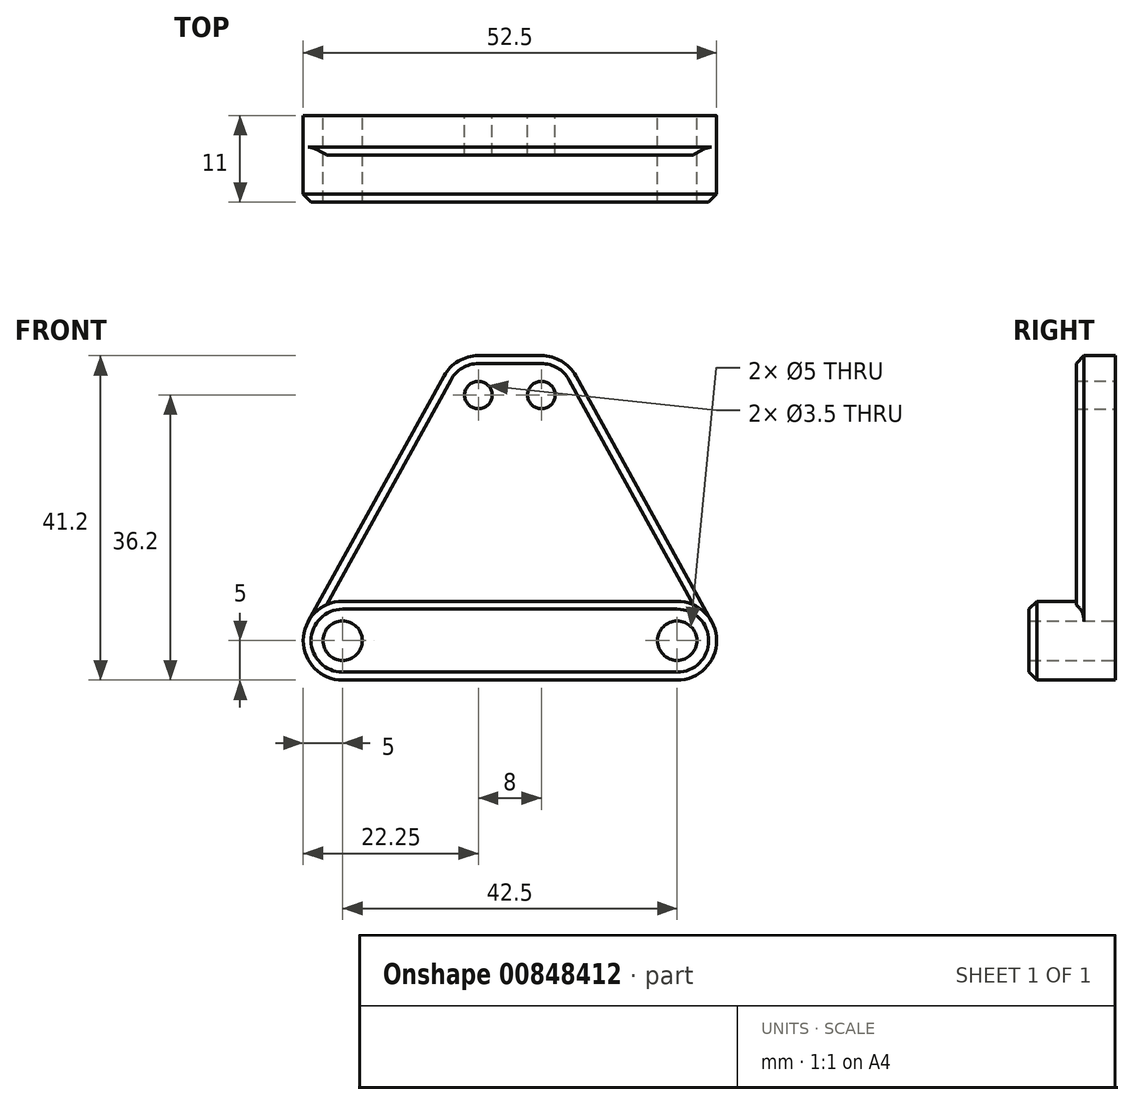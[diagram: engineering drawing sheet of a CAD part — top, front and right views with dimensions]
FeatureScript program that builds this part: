
annotation { "Feature Type Name" : "Feature", "Feature Type Description" : "" }
export const myFeature = defineFeature(function(context is Context, id is Id, definition is map)
    precondition{}
    {
        {
            var Q0;
            Q0=qCreatedBy(makeId("Front.planeOp"),FACE);
            var sketch = newSketch(context, id + "F0", { "sketchPlane" : qUnion([Q0])});
            skCircle(sketch, "E0", {"center": v(0, 0) * mm, "radius": 2.5 * mm});
            skCircle(sketch, "E1", {"center": v(42.5, 0) * mm, "radius": 2.5 * mm});
            skCircle(sketch, "E2", {"center": v(17.25, 31.2) * mm, "radius": 1.75 * mm});
            skCircle(sketch, "E3", {"center": v(25.25, 31.2) * mm, "radius": 1.75 * mm});
            skLineSegment(sketch, "E4", {"start": v(0, 0) * mm, "end": v(42.5, 0) * mm});
            skLineSegment(sketch, "E5", {"start": v(17.25, 31.2) * mm, "end": v(25.25, 31.2) * mm});
            skPoint(sketch, "E6", {"position": v(21.25, 31.2) * mm});
            skPoint(sketch, "E7", {"position": v(21.25, 0) * mm});
            skArc(sketch, "E8", {"start": v(-4.38, 2.42) * mm, "mid": v(-4.3, -2.54) * mm, "end": v(0, -5) * mm});
            skArc(sketch, "E9", {"start": v(42.5, -5) * mm, "mid": v(46.8, -2.54) * mm, "end": v(46.88, 2.42) * mm});
            skArc(sketch, "E10", {"start": v(17.25, 36.2) * mm, "mid": v(14.7, 35.5) * mm, "end": v(12.87, 33.62) * mm});
            skArc(sketch, "E11", {"start": v(29.63, 33.62) * mm, "mid": v(27.8, 35.5) * mm, "end": v(25.25, 36.2) * mm});
            skLineSegment(sketch, "E12", {"start": v(-4.38, 2.42) * mm, "end": v(12.87, 33.62) * mm});
            skLineSegment(sketch, "E13", {"start": v(17.25, 36.2) * mm, "end": v(25.25, 36.2) * mm});
            skLineSegment(sketch, "E14", {"start": v(29.63, 33.62) * mm, "end": v(46.88, 2.42) * mm});
            skLineSegment(sketch, "E15", {"start": v(42.5, -5) * mm, "end": v(0, -5) * mm});
            skSolve(sketch);
        }
        {
            var Q0;
            Q0=makeQuery(id+"F0.imprint","IMPRINT",FACE,{"disambiguationData":[TD([[makeQuery(id+"F0.imprint","IMPRINT",EDGE,{"derivedFrom":sQuery(id+"F0.wireOp",EDGE,"E0")}),-1.0]])]});
            extrude(context, id + "F1", {"entities" : qUnion([Q0]), "depth" : 5 * mm, "offsetDistance" : 25 * mm});
        }
        {
            var Q0;
            Q0=makeQuery(id+"F1.opExtrude","CAP_FACE",FACE,{"disambiguationData":[OSD([sQuery(id+"F0.wireOp",EDGE,"E0"),sQuery(id+"F0.wireOp",EDGE,"E1"),sQuery(id+"F0.wireOp",EDGE,"E2"),sQuery(id+"F0.wireOp",EDGE,"E3"),sQuery(id+"F0.wireOp",EDGE,"E8"),sQuery(id+"F0.wireOp",EDGE,"E9"),sQuery(id+"F0.wireOp",EDGE,"E10"),sQuery(id+"F0.wireOp",EDGE,"E11"),sQuery(id+"F0.wireOp",EDGE,"E12"),sQuery(id+"F0.wireOp",EDGE,"E13"),sQuery(id+"F0.wireOp",EDGE,"E14"),sQuery(id+"F0.wireOp",EDGE,"E15")])],"isStart":false});
            var sketch = newSketch(context, id + "F2", { "sketchPlane" : qUnion([Q0])});
            skLineSegment(sketch, "E16.0.0", {"start": v(46.88, 2.42) * mm, "end": v(29.63, 33.62) * mm});
            skArc(sketch, "E16.0.1", {"start": v(29.63, 33.62) * mm, "mid": v(27.8, 35.5) * mm, "end": v(25.25, 36.2) * mm});
            skLineSegment(sketch, "E16.0.2", {"start": v(25.25, 36.2) * mm, "end": v(17.25, 36.2) * mm});
            skArc(sketch, "E16.0.3", {"start": v(17.25, 36.2) * mm, "mid": v(14.7, 35.5) * mm, "end": v(12.87, 33.62) * mm});
            skLineSegment(sketch, "E16.0.4", {"start": v(12.87, 33.62) * mm, "end": v(-4.38, 2.42) * mm});
            skArc(sketch, "E16.0.5", {"start": v(-4.38, 2.42) * mm, "mid": v(-4.3, -2.54) * mm, "end": v(0, -5) * mm});
            skLineSegment(sketch, "E16.0.6", {"start": v(0, -5) * mm, "end": v(42.5, -5) * mm});
            skArc(sketch, "E16.0.7", {"start": v(42.5, -5) * mm, "mid": v(46.8, -2.54) * mm, "end": v(46.88, 2.42) * mm});
            skLineSegment(sketch, "E17", {"start": v(0, 5) * mm, "end": v(42.5, 5) * mm});
            skArc(sketch, "E18", {"start": v(0, 5) * mm, "mid": v(-5, 0) * mm, "end": v(0, -5) * mm});
            skArc(sketch, "E19", {"start": v(42.5, -5) * mm, "mid": v(47.5, 0) * mm, "end": v(42.5, 5) * mm});
            skSolve(sketch);
        }
        {
            var Q0;
            {var subQ3=sQuery(id+"F2.wireOp",EDGE,"E16.0.6");Q0=makeQuery(id+"F2.imprint","IMPRINT",FACE,{"disambiguationData":[TD([[makeQuery(id+"F2.imprint","IMPRINT",EDGE,{"derivedFrom":subQ3}),-1.0]])]});}
            extrude(context, id + "F3", {"entities" : qUnion([Q0]), "operationType" : NewBodyOperationType.ADD, "depth" : 6 * mm, "offsetDistance" : 25 * mm});
        }
        {
            var Q0;
            Q0=makeQuery(id+"F3.opExtrude","CAP_EDGE",EDGE,{"disambiguationData":[OSD([sQuery(id+"F2.wireOp",EDGE,"E17")])],"isStart":false});
            var Q1;
            Q1=makeQuery(id+"F1.opExtrude","CAP_EDGE",EDGE,{"disambiguationData":[OSD([sQuery(id+"F0.wireOp",EDGE,"E14")])],"isStart":false});
            chamfer(context, id + "F4", {"entities" : qUnion([Q0, Q1]), "width" : 1 * mm, "tangentPropagation" : true});
        }
    });
